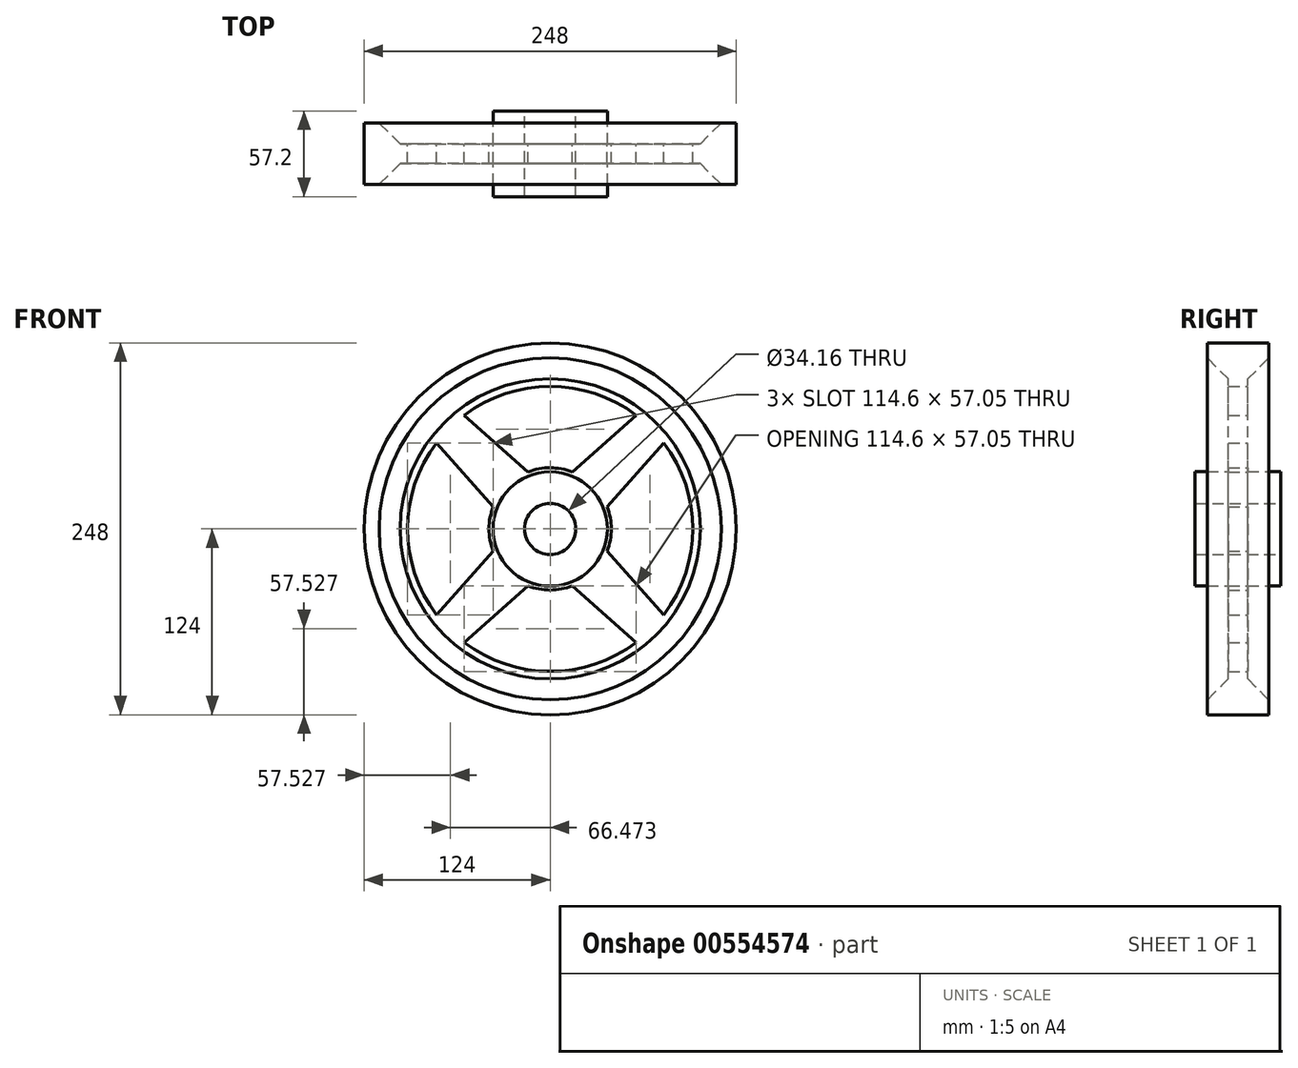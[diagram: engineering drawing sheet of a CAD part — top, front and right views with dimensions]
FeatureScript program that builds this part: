
annotation { "Feature Type Name" : "Feature", "Feature Type Description" : "" }
export const myFeature = defineFeature(function(context is Context, id is Id, definition is map)
    precondition{}
    {
        {
            var Q0;
            Q0=qCreatedBy(makeId("Front.planeOp"),FACE);
            var sketch = newSketch(context, id + "F0", { "sketchPlane" : qUnion([Q0])});
            skCircle(sketch, "E0", {"center": v(0, 0) * mm, "radius": 17.08 * mm});
            skCircle(sketch, "E1", {"center": v(0, 0) * mm, "radius": 38.1 * mm});
            skCircle(sketch, "E2", {"center": v(0, 0) * mm, "radius": 124 * mm});
            skCircle(sketch, "E3", {"center": v(0, 0) * mm, "radius": 114 * mm});
            skCircle(sketch, "E4", {"center": v(0, 0) * mm, "radius": 100 * mm});
            skArc(sketch, "E5", {"start": v(-75.77, 57.3) * mm, "mid": v(-95, 0) * mm, "end": v(-75.77, -57.3) * mm});
            skArc(sketch, "E6", {"start": v(-37.95, 14.84) * mm, "mid": v(-40.74, 0.02) * mm, "end": v(-37.96, -14.8) * mm});
            skLineSegment(sketch, "E7", {"start": v(-14.84, -37.95) * mm, "end": v(-57.3, -75.77) * mm});
            skLineSegment(sketch, "E8", {"start": v(14.78, -37.97) * mm, "end": v(14.77, -37.95) * mm});
            skLineSegment(sketch, "E9", {"start": v(14.77, -37.95) * mm, "end": v(57.3, -75.77) * mm});
            skPoint(sketch, "E10.start.orphan", {"position": v(0, -95) * mm});
            skPoint(sketch, "E11.start.orphan", {"position": v(0, -40.74) * mm});
            skLineSegment(sketch, "E12.1.0", {"start": v(-37.95, 14.84) * mm, "end": v(-75.77, 57.3) * mm});
            skLineSegment(sketch, "E12.1.1", {"start": v(-37.95, -14.77) * mm, "end": v(-75.77, -57.3) * mm});
            skArc(sketch, "E12.1.3", {"start": v(-57.3, -75.77) * mm, "mid": v(0, -95) * mm, "end": v(57.3, -75.77) * mm});
            skLineSegment(sketch, "E12.2.0", {"start": v(14.84, 37.95) * mm, "end": v(57.3, 75.77) * mm});
            skLineSegment(sketch, "E12.2.1", {"start": v(-14.77, 37.95) * mm, "end": v(-57.3, 75.77) * mm});
            skArc(sketch, "E12.2.3", {"start": v(-57.3, -75.77) * mm, "mid": v(0, -95) * mm, "end": v(57.3, -75.77) * mm});
            skLineSegment(sketch, "E12.3.0", {"start": v(37.95, -14.84) * mm, "end": v(75.77, -57.3) * mm});
            skLineSegment(sketch, "E12.3.1", {"start": v(37.95, 14.77) * mm, "end": v(75.77, 57.3) * mm});
            skArc(sketch, "E12.3.3", {"start": v(-57.3, -75.77) * mm, "mid": v(0, -95) * mm, "end": v(57.3, -75.77) * mm});
            skArc(sketch, "E13.trimOffspring", {"start": v(14.84, 37.95) * mm, "mid": v(0.02, 40.74) * mm, "end": v(-14.8, 37.96) * mm});
            skArc(sketch, "E14.trimOffspring", {"start": v(-14.84, -37.95) * mm, "mid": v(-0.02, -40.74) * mm, "end": v(14.8, -37.96) * mm});
            skArc(sketch, "E15.trimOffspring", {"start": v(37.95, -14.84) * mm, "mid": v(40.74, -0.02) * mm, "end": v(37.96, 14.8) * mm});
            skArc(sketch, "E16.trimOffspring", {"start": v(75.77, -57.3) * mm, "mid": v(95, 0) * mm, "end": v(75.77, 57.3) * mm});
            skArc(sketch, "E17.trimOffspring", {"start": v(57.3, 75.77) * mm, "mid": v(0, 95) * mm, "end": v(-57.3, 75.77) * mm});
            skSolve(sketch);
        }
        {
            var Q0;
            Q0=makeQuery(id+"F0.imprint","IMPRINT",FACE,{"disambiguationData":[TD([[makeQuery(id+"F0.imprint","IMPRINT",EDGE,{"derivedFrom":sQuery(id+"F0.wireOp",EDGE,"E0")}),-1.0]])]});
            extrude(context, id + "F1", {"entities" : qUnion([Q0]), "endBound" : BoundingType.SYMMETRIC, "depth" : 57.2 * mm, "offsetDistance" : 25 * mm});
        }
        {
            var Q0;
            Q0=makeQuery(id+"F0.imprint","IMPRINT",FACE,{"disambiguationData":[TD([[makeQuery(id+"F0.imprint","IMPRINT",EDGE,{"derivedFrom":sQuery(id+"F0.wireOp",EDGE,"E1")}),-1.0]])]});
            extrude(context, id + "F2", {"entities" : qUnion([Q0]), "operationType" : NewBodyOperationType.ADD, "endBound" : BoundingType.SYMMETRIC, "depth" : 13 * mm, "offsetDistance" : 25 * mm});
        }
        {
            var Q0;
            Q0=makeQuery(id+"F0.imprint","IMPRINT",FACE,{"disambiguationData":[TD([[makeQuery(id+"F0.imprint","IMPRINT",EDGE,{"derivedFrom":sQuery(id+"F0.wireOp",EDGE,"E3")}),1.0]])]});
            extrude(context, id + "F3", {"entities" : qUnion([Q0]), "operationType" : NewBodyOperationType.ADD, "endBound" : BoundingType.SYMMETRIC, "depth" : 41 * mm, "offsetDistance" : 25 * mm});
        }
        {
            var Q0;
            Q0=makeQuery(id+"F3.opExtrude","CAP_EDGE",EDGE,{"disambiguationData":[OSD([sQuery(id+"F0.wireOp",EDGE,"E4")])],"isStart":false});
            var Q1;
            Q1=makeQuery(id+"F3.opExtrude","CAP_EDGE",EDGE,{"disambiguationData":[OSD([sQuery(id+"F0.wireOp",EDGE,"E4")])],"isStart":true});
            chamfer(context, id + "F4", {"entities" : qUnion([Q0, Q1]), "width" : 14 * mm, "tangentPropagation" : true});
        }
        {
            var Q0;
            Q0=makeQuery(id+"F0.imprint","IMPRINT",FACE,{"disambiguationData":[TD([[makeQuery(id+"F0.imprint","IMPRINT",EDGE,{"derivedFrom":sQuery(id+"F0.wireOp",EDGE,"E2")}),1.0]])]});
            extrude(context, id + "F5", {"entities" : qUnion([Q0]), "operationType" : NewBodyOperationType.ADD, "endBound" : BoundingType.SYMMETRIC, "depth" : 41 * mm, "offsetDistance" : 25 * mm});
        }
    });
